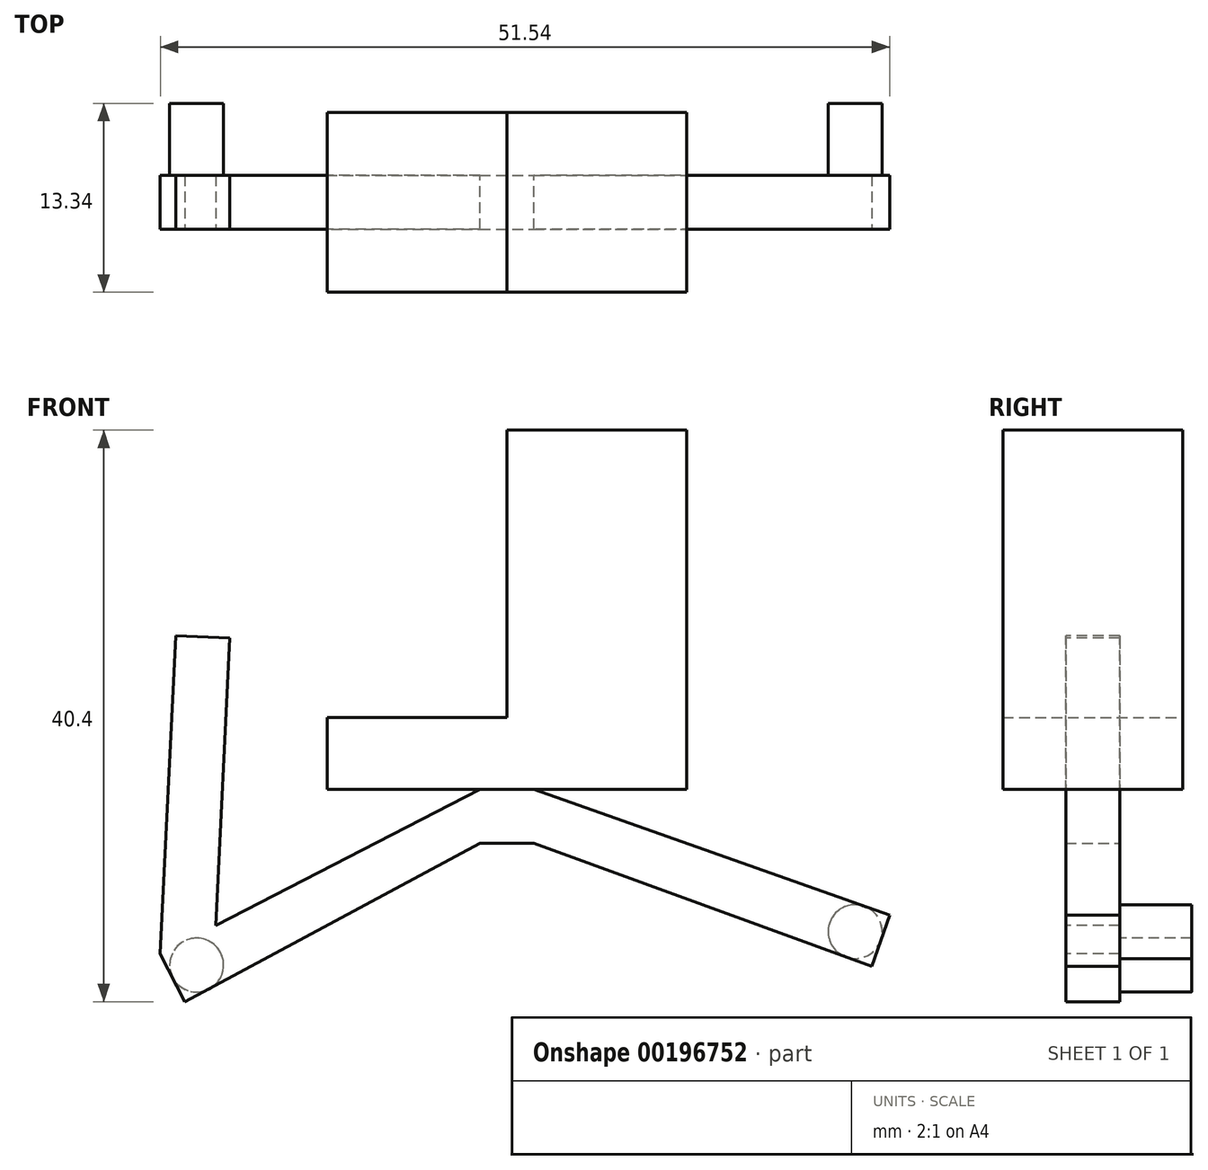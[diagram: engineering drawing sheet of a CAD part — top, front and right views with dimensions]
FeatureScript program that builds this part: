
annotation { "Feature Type Name" : "Feature", "Feature Type Description" : "" }
export const myFeature = defineFeature(function(context is Context, id is Id, definition is map)
    precondition{}
    {
        {
            var Q0;
            Q0=qCreatedBy(makeId("Front.planeOp"),FACE);
            var sketch = newSketch(context, id + "F0", { "sketchPlane" : qUnion([Q0])});
            skLineSegment(sketch, "E0.bottom", {"start": v(0, 0) * mm, "end": v(-12.7, 0) * mm});
            skLineSegment(sketch, "E0.top", {"start": v(0, 5.08) * mm, "end": v(-12.7, 5.08) * mm});
            skLineSegment(sketch, "E0.left", {"start": v(0, 0) * mm, "end": v(0, 5.08) * mm});
            skLineSegment(sketch, "E0.right", {"start": v(-12.7, 0) * mm, "end": v(-12.7, 5.08) * mm});
            skLineSegment(sketch, "E1.bottom", {"start": v(0, 0) * mm, "end": v(12.7, 0) * mm});
            skLineSegment(sketch, "E1.top", {"start": v(0, 25.4) * mm, "end": v(12.7, 25.4) * mm});
            skLineSegment(sketch, "E1.left", {"start": v(0, 0) * mm, "end": v(0, 25.4) * mm});
            skLineSegment(sketch, "E1.right", {"start": v(12.7, 0) * mm, "end": v(12.7, 25.4) * mm});
            skSolve(sketch);
        }
        {
            var Q0;
            Q0 = qSketchRegion(id + "F0", true);
            extrude(context, id + "F1", {"entities" : qUnion([Q0]), "depth" : 12.7 * mm});
        }
        {
            var Q0;
            Q0=makeQuery(id+"F1.opExtrude","SWEPT_FACE",FACE,{"disambiguationData":[OSD([sQuery(id+"F0.wireOp",EDGE,"E0.bottom"),sQuery(id+"F0.wireOp",EDGE,"E1.bottom")])]});
            var sketch = newSketch(context, id + "F2", { "sketchPlane" : qUnion([Q0])});
            skLineSegment(sketch, "E2", {"start": v(-12.7, 12.7) * mm, "end": v(12.7, 0) * mm});
            skLineSegment(sketch, "E3", {"start": v(-12.7, 0) * mm, "end": v(12.7, 12.7) * mm});
            skLineSegment(sketch, "E4.bottom", {"start": v(-1.9, 8.26) * mm, "end": v(1.9, 8.26) * mm});
            skLineSegment(sketch, "E4.top", {"start": v(-1.9, 4.45) * mm, "end": v(1.9, 4.45) * mm});
            skLineSegment(sketch, "E4.left", {"start": v(-1.9, 8.26) * mm, "end": v(-1.9, 4.45) * mm});
            skLineSegment(sketch, "E4.right", {"start": v(1.9, 8.26) * mm, "end": v(1.9, 4.45) * mm});
            skPoint(sketch, "E4.middle", {"position": v(0, 6.35) * mm});
            skSolve(sketch);
        }
        {
            var Q0;
            Q0 = qSketchRegion(id + "F2", true);
            extrude(context, id + "F3", {"entities" : qUnion([Q0]), "operationType" : NewBodyOperationType.ADD, "depth" : 3.8 * mm});
        }
        {
            var Q0;
            Q0=makeQuery(id+"F3.opExtrude","SWEPT_FACE",FACE,{"disambiguationData":[OSD([sQuery(id+"F2.wireOp",EDGE,"E4.bottom")])]});
            var sketch = newSketch(context, id + "F4", { "sketchPlane" : qUnion([Q0])});
            skLineSegment(sketch, "E5", {"start": v(-1.9, 0) * mm, "end": v(-24.5, -11.62) * mm});
            skLineSegment(sketch, "E6", {"start": v(-24.5, -11.62) * mm, "end": v(-22.75, -15) * mm});
            skLineSegment(sketch, "E7", {"start": v(-22.75, -15) * mm, "end": v(-1.9, -3.8) * mm});
            skLineSegment(sketch, "E8", {"start": v(1.9, 0) * mm, "end": v(27.05, -8.9) * mm});
            skLineSegment(sketch, "E9", {"start": v(27.05, -8.9) * mm, "end": v(25.78, -12.5) * mm});
            skLineSegment(sketch, "E10", {"start": v(25.78, -12.5) * mm, "end": v(1.9, -3.8) * mm});
            skLineSegment(sketch, "E11", {"start": v(1.9, 0) * mm, "end": v(-1.9, 0) * mm});
            skLineSegment(sketch, "E12", {"start": v(1.9, -3.81) * mm, "end": v(-1.9, -3.81) * mm});
            skSolve(sketch);
        }
        {
            var Q0;
            Q0 = qSketchRegion(id + "F4", true);
            extrude(context, id + "F5", {"entities" : qUnion([Q0]), "operationType" : NewBodyOperationType.ADD, "oppositeDirection" : true, "depth" : 3.8 * mm});
        }
        {
            var Q0;
            Q0=makeQuery(id+"F5.boolean.opBoolean","MERGE",FACE,{"derivedFrom":[makeQuery(id+"F3.opExtrude","SWEPT_FACE",FACE,{"disambiguationData":[OSD([sQuery(id+"F2.wireOp",EDGE,"E4.bottom")])]}),makeQuery(id+"F5.opExtrude","CAP_FACE",FACE,{"disambiguationData":[OSD([sQuery(id+"F4.wireOp",EDGE,"E5"),sQuery(id+"F4.wireOp",EDGE,"E6"),sQuery(id+"F4.wireOp",EDGE,"E7"),sQuery(id+"F4.wireOp",EDGE,"E8"),sQuery(id+"F4.wireOp",EDGE,"E9"),sQuery(id+"F4.wireOp",EDGE,"E10"),sQuery(id+"F4.wireOp",EDGE,"E11"),sQuery(id+"F4.wireOp",EDGE,"E12")])],"isStart":true})]});
            var sketch = newSketch(context, id + "F6", { "sketchPlane" : qUnion([Q0])});
            skLineSegment(sketch, "E13", {"start": v(-24.5, -11.62) * mm, "end": v(-23.4, 10.88) * mm});
            skLineSegment(sketch, "E14", {"start": v(-23.4, 10.88) * mm, "end": v(-19.6, 10.7) * mm});
            skLineSegment(sketch, "E15", {"start": v(-19.6, 10.7) * mm, "end": v(-20.58, -9.6) * mm});
            skLineSegment(sketch, "E16", {"start": v(-24.5, -11.62) * mm, "end": v(-20.58, -9.6) * mm});
            skSolve(sketch);
        }
        {
            var Q0;
            Q0 = qSketchRegion(id + "F6", true);
            extrude(context, id + "F7", {"entities" : qUnion([Q0]), "operationType" : NewBodyOperationType.ADD, "oppositeDirection" : true, "depth" : 3.8 * mm});
        }
        {
            var Q0;
            Q0=makeQuery(id+"F7.boolean.opBoolean","MERGE",FACE,{"derivedFrom":[makeQuery(id+"F5.boolean.opBoolean","MERGE",FACE,{"derivedFrom":[makeQuery(id+"F3.opExtrude","SWEPT_FACE",FACE,{"disambiguationData":[OSD([sQuery(id+"F2.wireOp",EDGE,"E4.top")])]}),makeQuery(id+"F5.opExtrude","CAP_FACE",FACE,{"disambiguationData":[OSD([sQuery(id+"F4.wireOp",EDGE,"E5"),sQuery(id+"F4.wireOp",EDGE,"E6"),sQuery(id+"F4.wireOp",EDGE,"E7"),sQuery(id+"F4.wireOp",EDGE,"E8"),sQuery(id+"F4.wireOp",EDGE,"E9"),sQuery(id+"F4.wireOp",EDGE,"E10"),sQuery(id+"F4.wireOp",EDGE,"E11"),sQuery(id+"F4.wireOp",EDGE,"E12")])],"isStart":false})]}),makeQuery(id+"F7.opExtrude","CAP_FACE",FACE,{"disambiguationData":[OSD([sQuery(id+"F6.wireOp",EDGE,"E13"),sQuery(id+"F6.wireOp",EDGE,"E14"),sQuery(id+"F6.wireOp",EDGE,"E15"),sQuery(id+"F6.wireOp",EDGE,"E16")])],"isStart":false})]});
            var sketch = newSketch(context, id + "F8", { "sketchPlane" : qUnion([Q0])});
            skPoint(sketch, "E17", {"position": v(-23.46, -7.63) * mm});
            skPoint(sketch, "E18", {"position": v(-22.2, -11.19) * mm});
            skLineSegment(sketch, "E19", {"start": v(-23.46, -7.63) * mm, "end": v(-25.78, -12.5) * mm});
            skLineSegment(sketch, "E20", {"start": v(-27.05, -8.9) * mm, "end": v(-22.2, -11.19) * mm});
            skCircle(sketch, "E21", {"center": v(-24.61, -10.05) * mm, "radius": 1.9 * mm});
            skLineSegment(sketch, "E22", {"start": v(20.58, -9.6) * mm, "end": v(21.1, -9.87) * mm});
            skPoint(sketch, "E23", {"position": v(19.4, -13.2) * mm});
            skPoint(sketch, "E24", {"position": v(21.1, -9.87) * mm});
            skLineSegment(sketch, "E25", {"start": v(21.1, -9.87) * mm, "end": v(22.75, -15) * mm});
            skLineSegment(sketch, "E26", {"start": v(19.4, -13.2) * mm, "end": v(24.5, -11.62) * mm});
            skCircle(sketch, "E27", {"center": v(21.92, -12.42) * mm, "radius": 1.9 * mm});
            skLineSegment(sketch, "E28.trimOffspring", {"start": v(22.56, -10.62) * mm, "end": v(23, -10.85) * mm});
            skSolve(sketch);
        }
        {
            var Q0;
            Q0 = qSketchRegion(id + "F8", true);
            extrude(context, id + "F9", {"entities" : qUnion([Q0]), "operationType" : NewBodyOperationType.ADD, "depth" : 5.08 * mm});
        }
    });
